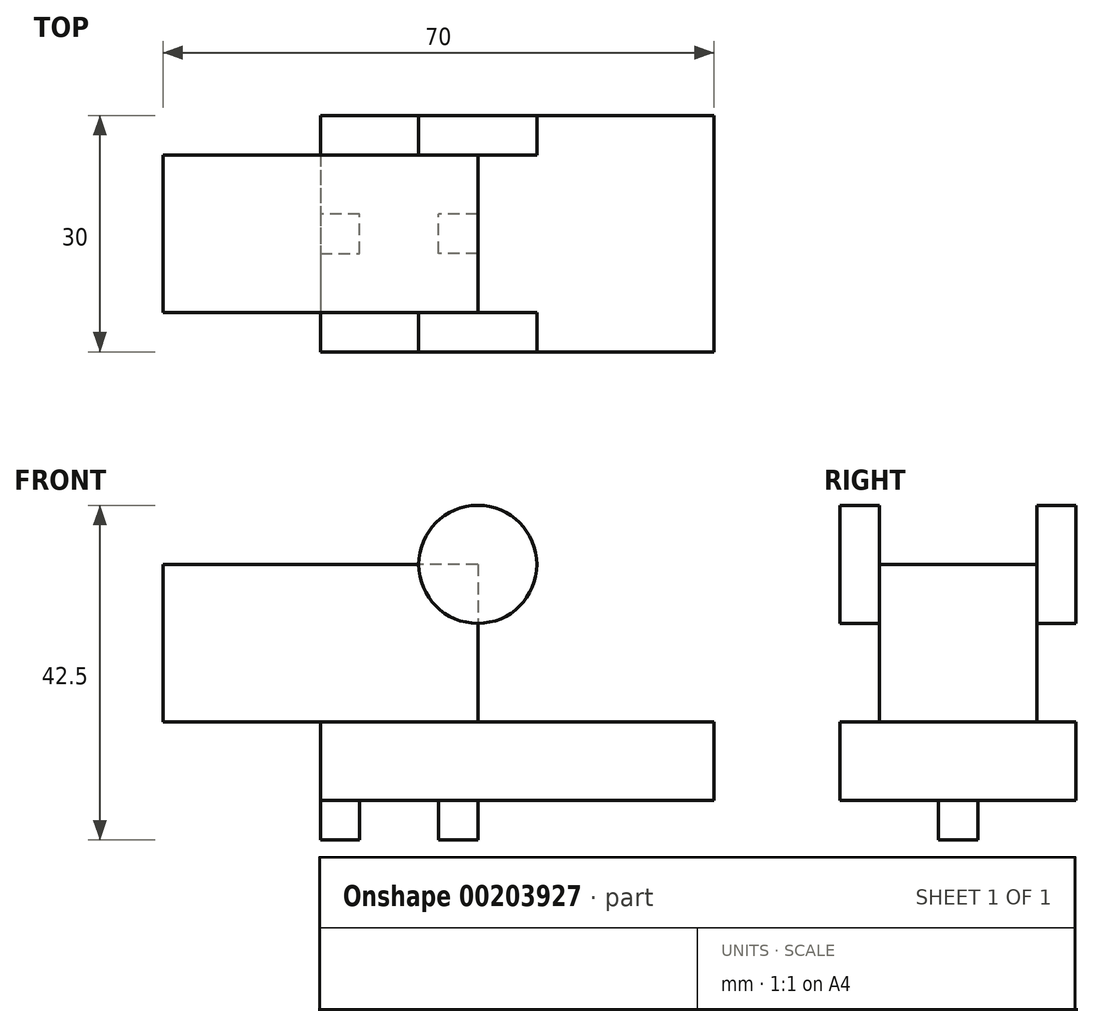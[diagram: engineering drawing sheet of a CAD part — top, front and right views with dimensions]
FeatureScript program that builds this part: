
annotation { "Feature Type Name" : "Feature", "Feature Type Description" : "" }
export const myFeature = defineFeature(function(context is Context, id is Id, definition is map)
    precondition{}
    {
        {
            var Q0;
            Q0=qCreatedBy(makeId("Top.planeOp"),FACE);
            var sketch = newSketch(context, id + "F0", { "sketchPlane" : qUnion([Q0])});
            skLineSegment(sketch, "E0.bottom", {"start": v(25, 15) * mm, "end": v(-25, 15) * mm});
            skLineSegment(sketch, "E0.top", {"start": v(25, -15) * mm, "end": v(-25, -15) * mm});
            skLineSegment(sketch, "E0.left", {"start": v(25, 15) * mm, "end": v(25, -15) * mm});
            skLineSegment(sketch, "E0.right", {"start": v(-25, 15) * mm, "end": v(-25, -15) * mm});
            skPoint(sketch, "E0.middle", {"position": v(0, 0) * mm});
            skSolve(sketch);
        }
        {
            var Q0;
            Q0=qSketchRegion(id+"F0",true);
            extrude(context, id + "F1", {"entities" : qUnion([Q0]), "depth" : 10 * mm});
        }
        {
            var Q0;
            Q0=makeQuery(id+"F1.opExtrude","CAP_FACE",FACE,{"disambiguationData":[OSD([sQuery(id+"F0.wireOp",EDGE,"E0.bottom"),sQuery(id+"F0.wireOp",EDGE,"E0.top"),sQuery(id+"F0.wireOp",EDGE,"E0.left"),sQuery(id+"F0.wireOp",EDGE,"E0.right")])],"isStart":true});
            var sketch = newSketch(context, id + "F2", { "sketchPlane" : qUnion([Q0])});
            skLineSegment(sketch, "E1", {"start": v(-25, 0) * mm, "end": v(-25, 2.5) * mm});
            skLineSegment(sketch, "E2", {"start": v(-25, 2.5) * mm, "end": v(-20, 2.5) * mm});
            skLineSegment(sketch, "E3", {"start": v(-20, 2.5) * mm, "end": v(-20, -2.5) * mm});
            skLineSegment(sketch, "E4", {"start": v(-20, -2.5) * mm, "end": v(-25, -2.5) * mm});
            skLineSegment(sketch, "E5", {"start": v(-25, -2.5) * mm, "end": v(-25, 0) * mm});
            skLineSegment(sketch, "E6.bottom", {"start": v(-5, 2.5) * mm, "end": v(-10, 2.5) * mm});
            skLineSegment(sketch, "E6.top", {"start": v(-5, -2.5) * mm, "end": v(-10, -2.5) * mm});
            skLineSegment(sketch, "E6.left", {"start": v(-5, 2.5) * mm, "end": v(-5, -2.5) * mm});
            skLineSegment(sketch, "E6.right", {"start": v(-10, 2.5) * mm, "end": v(-10, -2.5) * mm});
            skPoint(sketch, "E6.middle", {"position": v(-7.5, 0) * mm});
            skLineSegment(sketch, "E7", {"start": v(-25, 0) * mm, "end": v(-22.5, 0) * mm, "construction": true});
            skSolve(sketch);
        }
        {
            var Q0;
            Q0=qSketchRegion(id+"F2",true);
            extrude(context, id + "F3", {"entities" : qUnion([Q0]), "operationType" : NewBodyOperationType.ADD, "depth" : 5 * mm});
        }
        {
            var Q0;
            Q0=makeQuery(id+"F1.opExtrude","CAP_FACE",FACE,{"disambiguationData":[OSD([sQuery(id+"F0.wireOp",EDGE,"E0.bottom"),sQuery(id+"F0.wireOp",EDGE,"E0.top"),sQuery(id+"F0.wireOp",EDGE,"E0.left"),sQuery(id+"F0.wireOp",EDGE,"E0.right")])],"isStart":false});
            var sketch = newSketch(context, id + "F4", { "sketchPlane" : qUnion([Q0])});
            skLineSegment(sketch, "E8", {"start": v(-25, 10) * mm, "end": v(-5, 10) * mm});
            skLineSegment(sketch, "E9", {"start": v(-5, 10) * mm, "end": v(-5, -10) * mm});
            skLineSegment(sketch, "E10", {"start": v(-5, -10) * mm, "end": v(-25, -10) * mm});
            skLineSegment(sketch, "E11", {"start": v(-25, -10) * mm, "end": v(-25, 0) * mm});
            skLineSegment(sketch, "E12", {"start": v(-25, 0) * mm, "end": v(-25, 10) * mm});
            skSolve(sketch);
        }
        {
            var Q0;
            Q0=qSketchRegion(id+"F4",true);
            extrude(context, id + "F5", {"entities" : qUnion([Q0]), "operationType" : NewBodyOperationType.ADD, "depth" : 20 * mm});
        }
        {
            var Q0;
            Q0=makeQuery(id+"F5.boolean.opBoolean","MERGE",FACE,{"derivedFrom":[makeQuery(id+"F3.boolean.opBoolean","MERGE",FACE,{"derivedFrom":[makeQuery(id+"F1.opExtrude","SWEPT_FACE",FACE,{"disambiguationData":[OSD([sQuery(id+"F0.wireOp",EDGE,"E0.right")])]}),makeQuery(id+"F3.opExtrude","SWEPT_FACE",FACE,{"disambiguationData":[OSD([sQuery(id+"F2.wireOp",EDGE,"E1"),sQuery(id+"F2.wireOp",EDGE,"E5")])]})]}),makeQuery(id+"F5.opExtrude","SWEPT_FACE",FACE,{"disambiguationData":[OSD([sQuery(id+"F4.wireOp",EDGE,"E11"),sQuery(id+"F4.wireOp",EDGE,"E12")])]})]});
            var sketch = newSketch(context, id + "F6", { "sketchPlane" : qUnion([Q0])});
            skPoint(sketch, "E13.endSnap0", {"position": v(0, 30) * mm});
            skLineSegment(sketch, "E14.bottom", {"start": v(-10, 30) * mm, "end": v(10, 30) * mm});
            skLineSegment(sketch, "E14.top", {"start": v(-10, 10) * mm, "end": v(10, 10) * mm});
            skLineSegment(sketch, "E14.left", {"start": v(-10, 30) * mm, "end": v(-10, 10) * mm});
            skLineSegment(sketch, "E14.right", {"start": v(10, 30) * mm, "end": v(10, 10) * mm});
            skSolve(sketch);
        }
        {
            var Q0;
            Q0=qSketchRegion(id+"F6",true);
            extrude(context, id + "F7", {"entities" : qUnion([Q0]), "operationType" : NewBodyOperationType.ADD, "depth" : 20 * mm});
        }
        {
            var Q0;
            Q0=makeQuery(id+"F7.boolean.opBoolean","MERGE",FACE,{"derivedFrom":[makeQuery(id+"F5.opExtrude","SWEPT_FACE",FACE,{"disambiguationData":[OSD([sQuery(id+"F4.wireOp",EDGE,"E10")])]}),makeQuery(id+"F7.opExtrude","SWEPT_FACE",FACE,{"disambiguationData":[OSD([sQuery(id+"F6.wireOp",EDGE,"E14.right")])]})]});
            var sketch = newSketch(context, id + "F8", { "sketchPlane" : qUnion([Q0])});
            skCircle(sketch, "E15", {"center": v(-5, 30) * mm, "radius": 7.5 * mm});
            skSolve(sketch);
        }
        {
            var Q0;
            Q0=qSketchRegion(id+"F8",true);
            extrude(context, id + "F9", {"entities" : qUnion([Q0]), "operationType" : NewBodyOperationType.ADD, "depth" : 5 * mm});
        }
        {
            var Q0;
            Q0=makeQuery(id+"F7.boolean.opBoolean","MERGE",FACE,{"derivedFrom":[makeQuery(id+"F5.opExtrude","SWEPT_FACE",FACE,{"disambiguationData":[OSD([sQuery(id+"F4.wireOp",EDGE,"E8")])]}),makeQuery(id+"F7.opExtrude","SWEPT_FACE",FACE,{"disambiguationData":[OSD([sQuery(id+"F6.wireOp",EDGE,"E14.left")])]})]});
            var sketch = newSketch(context, id + "F10", { "sketchPlane" : qUnion([Q0])});
            skCircle(sketch, "E16", {"center": v(5, 30) * mm, "radius": 7.5 * mm});
            skSolve(sketch);
        }
        {
            var Q0;
            Q0=qSketchRegion(id+"F10",true);
            extrude(context, id + "F11", {"entities" : qUnion([Q0]), "operationType" : NewBodyOperationType.ADD, "depth" : 5 * mm});
        }
    });
